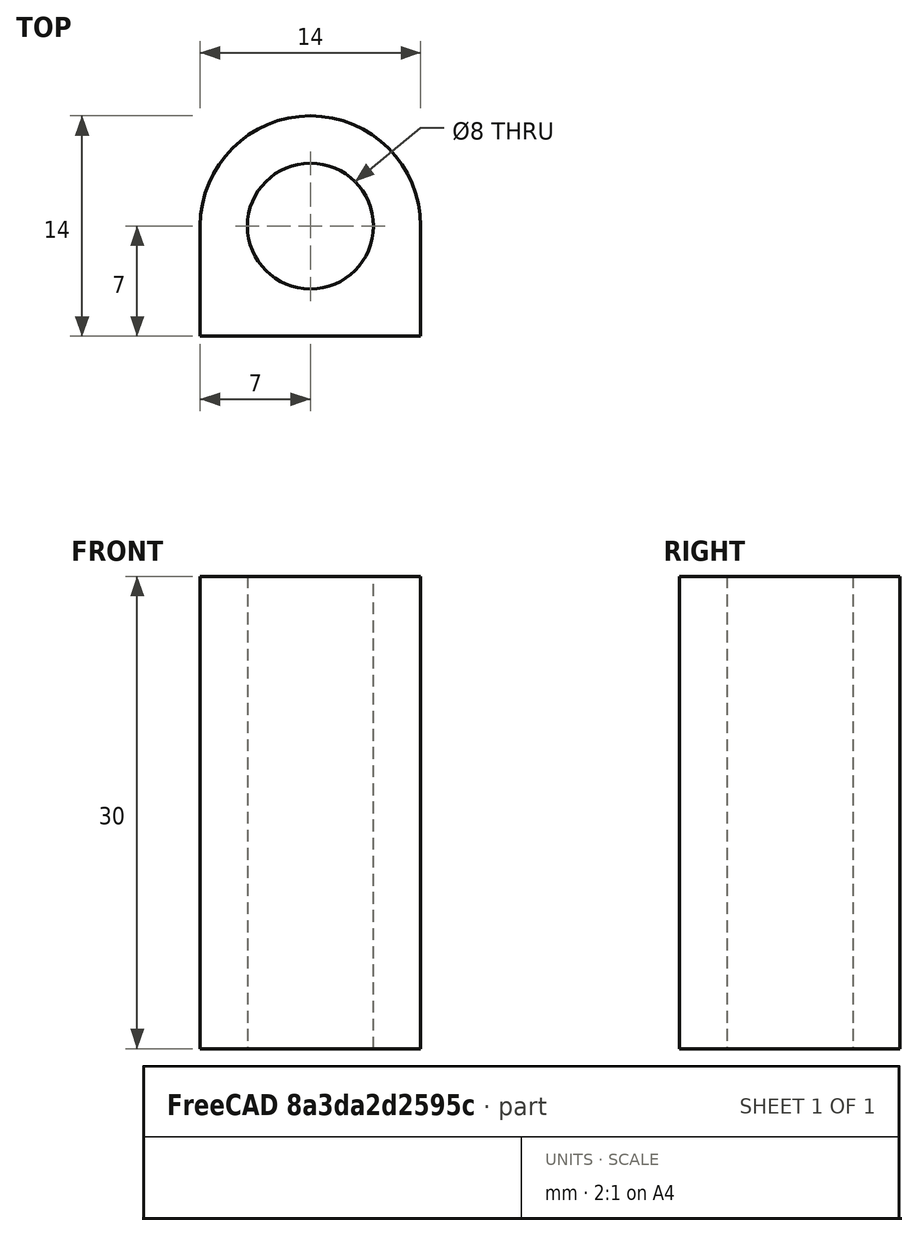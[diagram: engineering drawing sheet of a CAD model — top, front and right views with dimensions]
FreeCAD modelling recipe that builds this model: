
FCSTD DOCUMENT  (FreeCAD 0.19R24276 (Git))
Label: Trubka_30_v1
License: All rights reserved
LicenseURL: http://en.wikipedia.org/wiki/All_rights_reserved
objects: Sketcher::SketchObject×1, PartDesign::Pad×1, PartDesign::Body×1
note: 4 computed .brp shape members not serialized (recipe doc carries the construction recipe); baked Part::Feature solids carry a one-line shape summary decoded from their .brp

FEATURE [Sketcher::SketchObject] Sketch
  FullyConstrained = false
  MapMode = 5
  Support = -> [XY_Plane]
  sketch-geometry (5):
    g0: Circle CenterX=0 CenterY=0 CenterZ=0 NormalX=0 NormalY=0 NormalZ=1 AngleXU=0 Radius=4
    g1: ArcOfCircle CenterX=0 CenterY=0 CenterZ=0 NormalX=0 NormalY=0 NormalZ=1 AngleXU=0 Radius=7 StartAngle=1e-16 EndAngle=3.14159
    g2: LineSegment StartX=7 StartY=5e-16 StartZ=0 EndX=7 EndY=-7 EndZ=0
    g3: LineSegment StartX=7 StartY=-7 StartZ=0 EndX=-7 EndY=-7 EndZ=0
    g4: LineSegment StartX=-7 StartY=-7 StartZ=0 EndX=-7 EndY=0 EndZ=0
  constraints (13):
    c: Coincident(g0,g-1)
    c: Diameter(g0) = 8
    c: Coincident(g1,g-1)
    c: Diameter(g1) = 14
    c: Coincident(g2,g3)
    c: Coincident(g3,g4)
    c: Horizontal(g3)
    c: Vertical(g2)
    c: Vertical(g4)
    c: PointOnObject(g4,g-1)
    c: DistanceY(g2,g2) = 7
    c: DistanceX(g4,g-1) = 7
    c: Coincident(g1,g2)
FEATURE [PartDesign::Pad] Pad
  Direction = (1,1,1)
  Length = 30
  Length2 = 100
  Profile = -> Sketch
  Type = 0
FEATURE [PartDesign::Body] Body
  Group = -> [Sketch,Pad]
  Origin = -> Origin
  Tip = -> Pad
